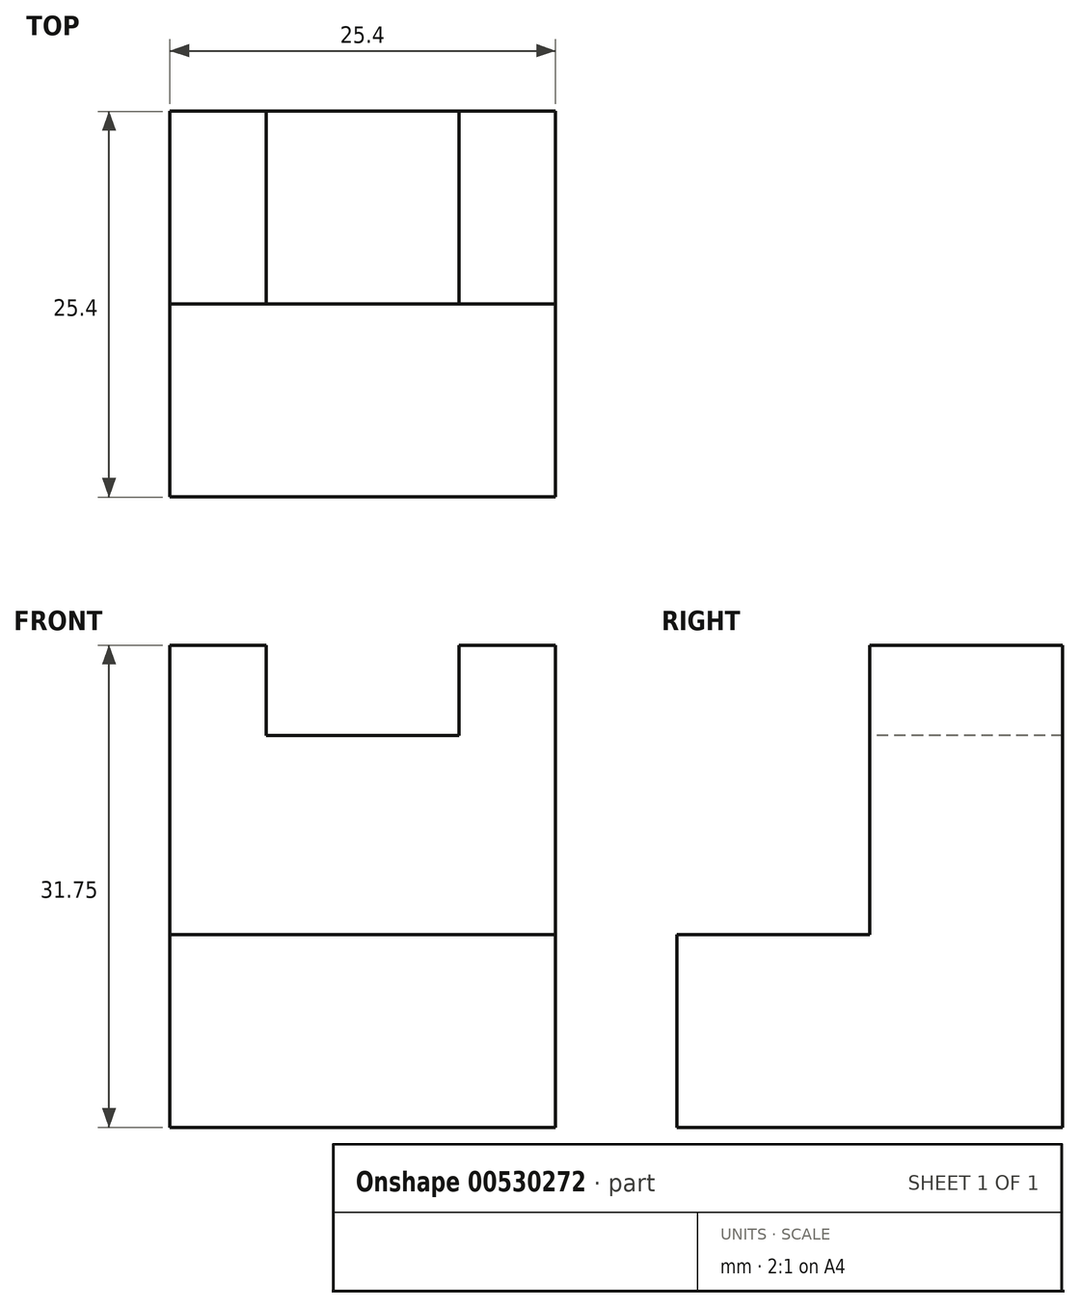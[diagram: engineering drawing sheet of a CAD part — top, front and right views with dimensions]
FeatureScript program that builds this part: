
annotation { "Feature Type Name" : "Feature", "Feature Type Description" : "" }
export const myFeature = defineFeature(function(context is Context, id is Id, definition is map)
    precondition{}
    {
        {
            var Q0;
            Q0=qCreatedBy(makeId("Right.planeOp"),FACE);
            var sketch = newSketch(context, id + "F0", { "sketchPlane" : qUnion([Q0])});
            skLineSegment(sketch, "E0", {"start": v(-50.84, 45.78) * mm, "end": v(-50.84, 14.03) * mm});
            skLineSegment(sketch, "E1", {"start": v(-50.84, 14.03) * mm, "end": v(-76.24, 14.03) * mm});
            skLineSegment(sketch, "E2", {"start": v(-76.24, 14.03) * mm, "end": v(-76.24, 26.73) * mm});
            skLineSegment(sketch, "E3", {"start": v(-76.24, 26.73) * mm, "end": v(-63.54, 26.73) * mm});
            skLineSegment(sketch, "E4", {"start": v(-63.54, 26.73) * mm, "end": v(-63.54, 45.78) * mm});
            skLineSegment(sketch, "E5", {"start": v(-63.54, 45.78) * mm, "end": v(-50.84, 45.78) * mm});
            skSolve(sketch);
        }
        {
            var Q0;
            Q0 = qSketchRegion(id + "F0", true);
            extrude(context, id + "F1", {"entities" : qUnion([Q0]), "depth" : 25.4 * mm, "offsetDistance" : 25.4 * mm});
        }
        {
            var Q0;
            Q0=makeQuery(id+"F1.opExtrude","SWEPT_FACE",FACE,{"disambiguationData":[OSD([sQuery(id+"F0.wireOp",EDGE,"E4")])]});
            var sketch = newSketch(context, id + "F2", { "sketchPlane" : qUnion([Q0])});
            skLineSegment(sketch, "E6", {"start": v(6.35, 45.78) * mm, "end": v(6.35, 39.83) * mm});
            skLineSegment(sketch, "E7", {"start": v(6.35, 39.83) * mm, "end": v(19.05, 39.83) * mm});
            skLineSegment(sketch, "E8", {"start": v(19.05, 39.83) * mm, "end": v(19.05, 45.78) * mm});
            skSolve(sketch);
        }
        {
            var Q0;
            {var subQ0=sQuery(id+"F2.wireOp",EDGE,"E6");Q0=makeQuery(id+"F2.imprint","IMPRINT",FACE,{"disambiguationData":[TD([[makeQuery(id+"F2.imprint","IMPRINT",EDGE,{"derivedFrom":subQ0}),1.0]])]});}
            extrude(context, id + "F3", {"entities" : qUnion([Q0]), "operationType" : NewBodyOperationType.REMOVE, "oppositeDirection" : true, "depth" : 25.4 * mm, "offsetDistance" : 25.4 * mm});
        }
    });
